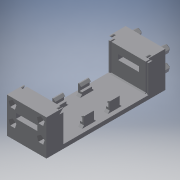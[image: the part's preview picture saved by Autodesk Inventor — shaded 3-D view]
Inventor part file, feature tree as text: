
AUTODESK INVENTOR PART (.ipt)
format: ipt  version: 2018 (Build 220112000, 112)  size: 414,720 bytes
history: native  units: mm
features: extrude x14, sketch x12, chamfer x5
ambient origin geometry x8: Origin, YZ Plane, XZ Plane, XY Plane, X Axis, Y Axis, Z Axis, Center Point
bodies: Solid1 (feature_tree)
feature tree (31):
  extrude  "Extrusion1"  Depth=50.0mm
  extrude  "Extrusion8"  Depth=8.5mm
  extrude  "Extrusion9"  Depth=4.67mm
  extrude  "Extrusion10"  Depth=2.54mm
  extrude  "Extrusion11"  Depth=5.73mm
  extrude  "Extrusion12"  Depth=8.5mm
  extrude  "Extrusion13"  Depth=8.5mm TaperAngle=0.0deg
  extrude  "Extrusion14"  Depth=0.7mm
  extrude  "Extrusion15"  Depth=0.6mm
  extrude  "Extrusion16"  Depth=0.7mm
  chamfer  "Chamfer4"  Distance=0.6mm
  extrude  "Extrusion19"  Depth=2.0mm TaperAngle=0.0deg
  extrude  "Extrusion20"  Depth=4.0mm TaperAngle=0.0deg
  extrude  "Extrusion21"  Depth=4.0mm TaperAngle=0.0deg
  extrude  "Extrusion22"  Depth=2.0mm
  chamfer  "Chamfer6"  Distance=1.8mm
  chamfer  "Chamfer7"  Distance=2.8mm
  chamfer  "Chamfer8"  Distance=2.4mm
  chamfer  "Chamfer9"  Distance=2.8mm
  sketch  "Sketch1"  dims[d0=20.0mm d1=50.0mm]
  sketch  "Sketch8"  dims[d2=2.0mm d3=0.0mm d39=8.5mm]
  sketch  "Sketch9"  dims[d40=16.0mm d41=0.0mm d42=4.67mm]
  sketch  "Sketch10"  dims[d43=4.67mm d45=2.54mm]
  sketch  "Sketch11"  dims[d46=8.5mm d47=0.0mm d48=5.73mm]
  sketch  "Sketch12"  dims[d49=10.0mm d50=0.0mm d51=8.5mm]
  sketch  "Sketch13"  dims[d52=16.0mm d53=0.0mm d58=8.5mm d59=0.0mm]
  sketch  "Sketch14"  dims[d63=0.6mm d64=0.7mm]
  sketch  "Sketch20"  dims[d65=0.7mm d66=0.6mm]
  sketch  "Sketch21"  dims[d67=2.0mm d68=0.0mm d69=0.7mm]
  sketch  "Sketch22"  dims[d70=0.7mm]
  sketch  "Sketch23"  dims[d71=0.6mm d72=0.6mm d73=2.0mm d74=0.0mm d83=4.0mm d84=0.0mm d85=4.0mm d86=0.0mm d95=2.4mm d96=1.8mm d97=2.8mm d98=2.4mm d99=1.8mm d100=2.8mm d101=2.4mm d102=2.4mm d141=2.15mm d142=2.15mm d143=2.15mm d144=2.15mm d145=0.5mm d146=2.0mm d147=45.0deg d148=16.0mm d149=18.0mm d150=2.0mm d151=12.5mm d152=5.0mm d153=0.0mm d154=2.0mm d155=2.0mm d156=2.0mm d157=2.0mm d158=0.8mm d159=2.0mm d160=0.8mm d161=2.0mm d162=1.5mm d163=1.5mm d164=18.0mm d165=0.0mm d169=8.0mm d170=5.0mm d171=18.0mm d172=0.0mm d173=2.0mm d174=2.0mm d175=2.0mm d176=18.0mm d177=0.0mm d178=1.0mm d179=2.0mm d180=45.0deg d181=1.0mm d182=2.0mm d183=45.0deg d184=8.14mm d185=8.14mm d186=2.93mm d187=2.87mm d188=0.25mm d189=2.0mm d190=45.0deg d191=14.26mm d192=0.5mm d193=2.0mm d194=45.0deg]
